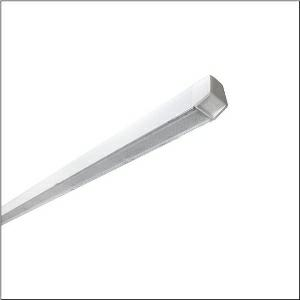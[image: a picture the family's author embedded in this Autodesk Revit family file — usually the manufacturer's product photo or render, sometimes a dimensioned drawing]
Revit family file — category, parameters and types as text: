
# Revit family: licross_r__11_recessed_ho_51ul1edv4m5r00s_7b8d
name_source: partatom
category: Lighting Fixtures
units: mm (PartAtom-declared; Revit-internal decimal feet)

## family parameters
Cut with Voids When Loaded = No
Host = Face
Light Source = No
Part Type = Normal
Room Calculation Point = No
Round Connector Dimension = Use Diameter
Shared = No

## types (1)
- --- (1 x LED, 25560 lm, 150.1 W, 4000K)
    Apparent Load = 150 VA
    CIE Flux Codes = 85 95 99 100 100
    Color Rendering = 80
    Color Temperature = 4000K
    Default Elevation = 1800 mm
    Description = Licross® 11 Recessed HO, single luminaire, primary optical cover: cover, of PMMA, light emission: direct distribution, primary light characteristic: symmetric, installation type: slip-in mounting, LED, rated luminous flux: 25.560lm, luminous efficacy: 170lm/W, light colour: 840, colour temperature: 4000K, control gear: ECG DALI, with terminal, 5-pole, max. 2.5mm², mains connection: 230V, AC, 50/60Hz, rated input power: 150W, Licross® LED insert, of sheet steel, galvanised, coil coated, white, length: 2.327mm, width: 70mm, height: 71mm, end cap, of PC, white, mounting rail, of sheet steel, galvanised, white, protection rating (complete): IP20, insulation class (complete): insulation class I (protective earthing), certification: CE, ENEC, VDE, UKCA, impact resistance: IK06, permissible operating ambient temperature: -35..+35°C, corresponds to IFS (International Featured Standards) requirements for safety and quality in the food industry, reducing of maximum allowable ambient temperature of 5°C with ceiling mounting, LABS conformity tested according to VDMA 24364:2018-05, packaging unit: 1 piece
    Height = 58 mm
    Lamp = 1 x LED
    Lamp Light Flux = 25560 lm
    Lamp Power = 150.1 W
    Lamp count = 1
    Length = 2250 mm
    Luminous efficacy = 170 lm/W
    Manufacturer = Siteco
    ModVariant = No
    Model = 51UL1EDV4M5R00S
    Mounting Place = Ceiling
    Mounting Type = Pendant
    Number of Poles = 1
    OnlyDefault = Yes
    Power Factor = 1
    Product Name = Licross® 11 Recessed HO
    Product group = single luminaire
    ProductGroupID = 909
    Protection Class = Protection class I
    Protection Degree = IP 20
    RLX_Detail_Level = 1
    RlxData = <blob elided: 32277 chars, md5=86956c69>
    Socket = socket
    Standby Power = 0 W
    System Light Flux = 25561 lm
    System Power = 150 W
    Type Comments = factory setting: luminous flux: 100 % | dim-lin: 254 | 575 mA
    Type Image = l_1006979.jpg
    URL = http://relux.com
    VarID = @adj_092671
    Voltage = 0 V
    Weight = 0.00 kg
    Width = 66 mm

## geometry (parser evidence)
native form markers: Blend x4, Sweep x10
no freeform markers — native parametric forms only
